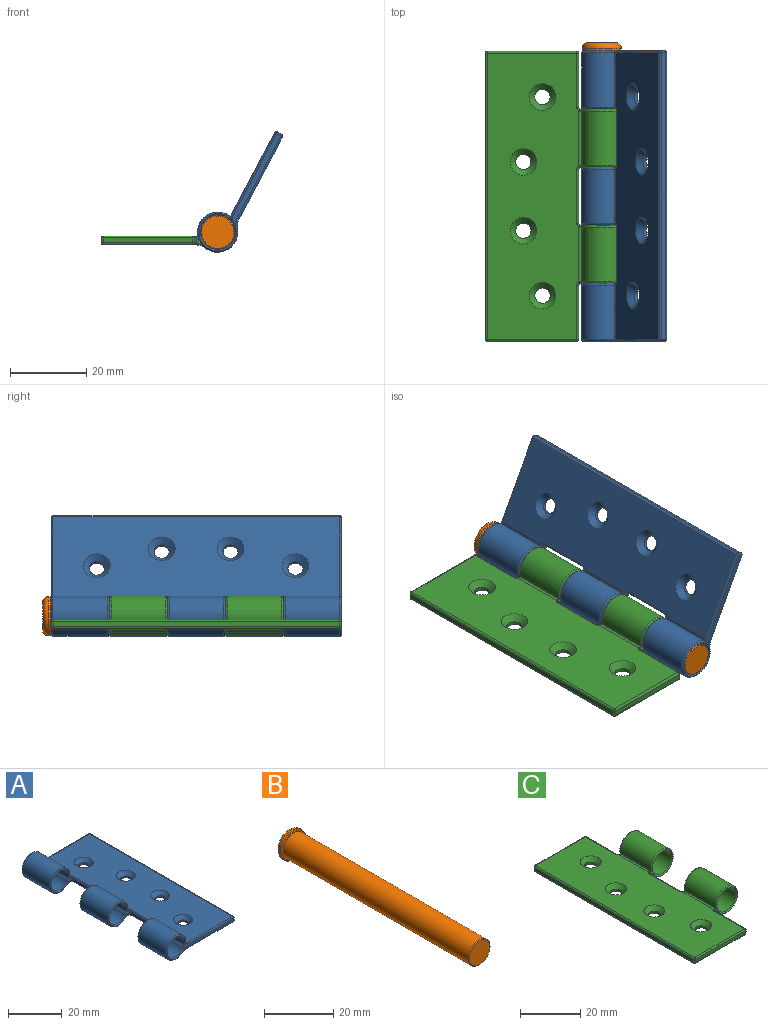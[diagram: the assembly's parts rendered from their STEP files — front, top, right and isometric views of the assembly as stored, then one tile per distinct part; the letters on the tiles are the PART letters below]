
ASSEMBLY  parts=3 mates=2
PART A: 94 faces, bbox 36.3x76x11.6 mm
  f0: cylinder r=5.25mm len=14.2mm, axis (0,1,0), area 412.4mm2, adj f2,f8,f69,f87
  f1: cylinder r=5.25mm len=14.2mm, axis (0,1,0), area 412.4mm2, adj f3,f9,f46,f78
  f2: plane 15.21x0.8mm, normal (0,0,-1), area 11.4mm2, adj f0,f4,f69,f71,f87,f90
  f3: plane 15.21x0.8mm, normal (0,0,-1), area 11.4mm2, adj f1,f5,f45,f46,f78,f80
  f4: cylinder r=4.5mm len=14.2mm, axis (0,1,0), area 382.9mm2, adj f2,f6,f71,f90
  f5: cylinder r=4.5mm len=14.2mm, axis (0,1,0), area 382.9mm2, adj f3,f7,f45,f80
  f6: cylinder r=2.39mm len=14.47mm, axis (0,1,0), area 36mm2, adj f4,f14,f73,f75,f92,f93
  f7: cylinder r=2.39mm len=14.33mm, axis (0,1,0), area 35.9mm2, adj f5,f14,f43,f82,f84
  f8: cylinder r=4.96mm len=14.47mm, axis (0,1,0), area 44.3mm2, adj f0,f16,f66,f68,f85,f88
  f9: cylinder r=4.96mm len=14.33mm, axis (0,1,0), area 44.3mm2, adj f1,f16,f48,f76,f77
  f10: cylinder r=5.25mm len=14.2mm, axis (0,1,0), area 412.4mm2, adj f11,f17,f51,f60
  f11: plane 15.21x0.8mm, normal (0,0,-1), area 11.4mm2, adj f10,f12,f51,f52,f60,f63
  f12: cylinder r=4.5mm len=14.2mm, axis (0,1,0), area 382.9mm2, adj f11,f13,f52,f63
  f13: cylinder r=2.39mm len=14.33mm, axis (0,1,0), area 35.9mm2, adj f12,f14,f49,f65,f67
  f14: plane 75x24mm, normal (0,0,1), area 1630.6mm2, adj f6,f7,f13,f21,f23,f25,f27,f41
  f15: plane 75x1.3mm, normal (1,0,0), area 97.5mm2, adj f38,f39,f42,f55
  f16: plane 75x24mm, normal (0,0,-1), area 1734.3mm2, adj f8,f9,f17,f20,f22,f24,f26,f50
  f17: cylinder r=4.96mm len=14.33mm, axis (0,1,0), area 44.3mm2, adj f10,f16,f54,f58,f61
  f18: plane 26.22x1.77mm, normal (0,-1,0), area 33.2mm2, adj f39,f47,f49,f52,f54,f56
  f19: plane 26.22x1.77mm, normal (0,1,0), area 33.2mm2, adj f38,f41,f43,f45,f48,f50
  f20: cylinder r=2mm len=4mm, axis (0,0,1), area 10.1mm2, adj f16,f21
  f21: cone r=2mm half-angle=45deg, axis (0,0,1), area 36.7mm2, adj f14,f20
  f22: cylinder r=2mm len=4mm, axis (0,0,1), area 10.1mm2, adj f16,f23
  f23: cone r=2mm half-angle=45deg, axis (0,0,1), area 36.7mm2, adj f14,f22
  f24: cylinder r=2mm len=4mm, axis (0,0,1), area 10.1mm2, adj f16,f25
  f25: cone r=2mm half-angle=45deg, axis (0,0,1), area 36.7mm2, adj f14,f24
  f26: cylinder r=2mm len=4mm, axis (0,0,1), area 10.1mm2, adj f16,f27
  f27: cone r=2mm half-angle=45deg, axis (0,0,1), area 36.7mm2, adj f14,f26
  f28: plane 14.2x1.3mm, normal (-1,0,0), area 18.5mm2, adj f34,f35,f81,f89
  f29: plane 1.72x1.7mm, normal (0,-1,0), area 1.3mm2, adj f34,f77,f80,f82
  f30: plane 1.72x1.7mm, normal (0,1,0), area 1.3mm2, adj f35,f88,f90,f92
  f31: plane 14.2x1.3mm, normal (-1,0,0), area 18.5mm2, adj f36,f37,f62,f72
  f32: plane 1.72x1.7mm, normal (0,1,0), area 1.3mm2, adj f36,f61,f63,f65
  f33: plane 1.72x1.7mm, normal (0,-1,0), area 1.3mm2, adj f37,f68,f71,f73
  f34: cylinder r=0.5mm len=1.32mm, axis (0,0,-1), area 1mm2, adj f28,f29,f76,f79,f84,f86
  f35: cylinder r=0.5mm len=1.32mm, axis (0,0,1), area 1mm2, adj f28,f30,f83,f85,f91,f93
  f36: cylinder r=0.5mm len=1.32mm, axis (0,0,-1), area 1mm2, adj f31,f32,f58,f59,f67,f70
  f37: cylinder r=0.5mm len=1.32mm, axis (0,0,1), area 1mm2, adj f31,f33,f64,f66,f74,f75
  f38: cylinder r=0.5mm len=1.3mm, axis (0,0,-1), area 1mm2, adj f15,f19,f40,f53
  f39: cylinder r=0.5mm len=1.3mm, axis (0,0,1), area 1mm2, adj f15,f18,f44,f57
  f40: sphere r=0.5mm, area 0.4mm2, adj f38,f41,f42
  f41: cylinder r=0.5mm len=24mm, axis (1,0,0), area 18.8mm2, adj f14,f19,f40,f43
  f42: cylinder r=0.5mm len=75mm, axis (0,1,0), area 58.9mm2, adj f14,f15,f40,f44
  f43: torus R=1.89mm, axis (0,-1,0), area 1.8mm2, adj f7,f19,f41,f45
  f44: sphere r=0.5mm, area 0.4mm2, adj f39,f42,f47
  f45: torus R=5mm, axis (0,-1,0), area 18.5mm2, adj f3,f5,f19,f43,f46,f48
  f46: torus R=4.75mm, axis (0,-1,0), area 18.7mm2, adj f1,f3,f45,f48
  f47: cylinder r=0.5mm len=24mm, axis (-1,0,0), area 18.8mm2, adj f14,f18,f44,f49
  f48: torus R=5.46mm, axis (0,-1,0), area 2.5mm2, adj f9,f19,f45,f46,f50
  f49: torus R=1.89mm, axis (0,-1,0), area 1.8mm2, adj f13,f18,f47,f52
  f50: cylinder r=0.5mm len=24mm, axis (-1,0,0), area 18.8mm2, adj f16,f19,f48,f53
  f51: torus R=4.75mm, axis (0,-1,0), area 18.7mm2, adj f10,f11,f52,f54
  f52: torus R=5mm, axis (0,-1,0), area 18.5mm2, adj f11,f12,f18,f49,f51,f54
  f53: sphere r=0.5mm, area 0.4mm2, adj f38,f50,f55
  f54: torus R=5.46mm, axis (0,-1,0), area 2.5mm2, adj f17,f18,f51,f52,f56
  f55: cylinder r=0.5mm len=75mm, axis (0,1,0), area 58.9mm2, adj f15,f16,f53,f57
  f56: cylinder r=0.5mm len=24mm, axis (1,0,0), area 18.8mm2, adj f16,f18,f54,f57
  f57: sphere r=0.5mm, area 0.4mm2, adj f39,f55,f56
  f58: bspline ~0.72x0.61mm, area 0.3mm2, adj f17,f36,f59,f61
  f59: torus R=1mm, axis (0,0,1), area 0.6mm2, adj f16,f36,f58,f62
  f60: torus R=4.75mm, axis (0,-1,0), area 18.7mm2, adj f10,f11,f61,f63
  f61: torus R=5.46mm, axis (0,-1,0), area 2.1mm2, adj f17,f32,f58,f60,f63
  f62: cylinder r=0.5mm len=14.2mm, axis (0,-1,0), area 11.2mm2, adj f16,f31,f59,f64
  f63: torus R=5mm, axis (0,-1,0), area 18.5mm2, adj f11,f12,f32,f60,f61,f65
  f64: torus R=1mm, axis (0,0,1), area 0.6mm2, adj f16,f37,f62,f66
  f65: torus R=1.89mm, axis (0,-1,0), area 1.4mm2, adj f13,f32,f63,f67
  f66: bspline ~0.72x0.61mm, area 0.3mm2, adj f8,f37,f64,f68
  f67: bspline ~0.83x0.6mm, area 0.3mm2, adj f13,f36,f65,f70
  f68: torus R=5.46mm, axis (0,-1,0), area 2.1mm2, adj f8,f33,f66,f69,f71
  f69: torus R=4.75mm, axis (0,-1,0), area 18.7mm2, adj f0,f2,f68,f71
  f70: torus R=1mm, axis (0,0,-1), area 0.6mm2, adj f14,f36,f67,f72
  f71: torus R=5mm, axis (0,-1,0), area 18.5mm2, adj f2,f4,f33,f68,f69,f73
  f72: cylinder r=0.5mm len=14.2mm, axis (0,-1,0), area 11.2mm2, adj f14,f31,f70,f74
  f73: torus R=1.89mm, axis (0,-1,0), area 1.4mm2, adj f6,f33,f71,f75
  f74: torus R=1mm, axis (0,0,-1), area 0.6mm2, adj f14,f37,f72,f75
  f75: bspline ~0.83x0.6mm, area 0.3mm2, adj f6,f37,f73,f74
  f76: bspline ~0.72x0.61mm, area 0.3mm2, adj f9,f34,f77,f79
  f77: torus R=5.46mm, axis (0,-1,0), area 2.1mm2, adj f9,f29,f76,f78,f80
  f78: torus R=4.75mm, axis (0,-1,0), area 18.7mm2, adj f1,f3,f77,f80
  f79: torus R=1mm, axis (0,0,1), area 0.6mm2, adj f16,f34,f76,f81
  f80: torus R=5mm, axis (0,-1,0), area 18.5mm2, adj f3,f5,f29,f77,f78,f82
  f81: cylinder r=0.5mm len=14.2mm, axis (0,1,0), area 11.2mm2, adj f16,f28,f79,f83
  f82: torus R=1.89mm, axis (0,-1,0), area 1.4mm2, adj f7,f29,f80,f84
  f83: torus R=1mm, axis (0,0,1), area 0.6mm2, adj f16,f35,f81,f85
  f84: bspline ~0.83x0.6mm, area 0.3mm2, adj f7,f34,f82,f86
  f85: bspline ~0.72x0.61mm, area 0.3mm2, adj f8,f35,f83,f88
  f86: torus R=1mm, axis (0,0,-1), area 0.6mm2, adj f14,f34,f84,f89
  f87: torus R=4.75mm, axis (0,-1,0), area 18.7mm2, adj f0,f2,f88,f90
  f88: torus R=5.46mm, axis (0,-1,0), area 2.1mm2, adj f8,f30,f85,f87,f90
  f89: cylinder r=0.5mm len=14.2mm, axis (0,-1,0), area 11.2mm2, adj f14,f28,f86,f91
  f90: torus R=5mm, axis (0,-1,0), area 18.5mm2, adj f2,f4,f30,f87,f88,f92
  f91: torus R=1mm, axis (0,0,-1), area 0.6mm2, adj f14,f35,f89,f93
  f92: torus R=1.89mm, axis (0,-1,0), area 1.4mm2, adj f6,f30,f90,f93
  f93: bspline ~0.83x0.6mm, area 0.3mm2, adj f6,f35,f91,f92
PART B: 8 faces, bbox 11x78.2x11 mm
  f0: cylinder r=4.4mm len=75.8mm, axis (0,1,0), area 2095.6mm2, adj f2,f5
  f1: plane 8.4x8.4mm, normal (0,-1,0), area 55.4mm2, adj f2
  f2: torus R=4.2mm, axis (0,-1,0), area 8.5mm2, adj f0,f1
  f3: cylinder r=5.1mm len=10.21mm, axis (0,-1,0), area 16mm2, adj f6,f7
  f4: plane 7.21x7.21mm, normal (0,1,0), area 40.8mm2, adj f6
  f5: plane 9.81x9.81mm, normal (0,-1,0), area 14.7mm2, adj f0,f7
  f6: torus R=3.6mm, axis (0,1,0), area 67.5mm2, adj f3,f4
  f7: torus R=4.9mm, axis (0,1,0), area 9.9mm2, adj f3,f5
PART C: 90 faces, bbox 36.3x76x11.6 mm
  f0: cylinder r=5.25mm len=14.2mm, axis (0,1,0), area 412.4mm2, adj f2,f8,f59,f83
  f1: cylinder r=5.25mm len=14.2mm, axis (0,1,0), area 412.4mm2, adj f3,f9,f46,f74
  f2: plane 15.21x0.8mm, normal (0,0,-1), area 11.4mm2, adj f0,f4,f59,f61,f83,f86
  f3: plane 15.21x0.8mm, normal (0,0,-1), area 11.4mm2, adj f1,f5,f46,f49,f74,f76
  f4: cylinder r=4.5mm len=14.2mm, axis (0,1,0), area 382.9mm2, adj f2,f6,f61,f86
  f5: cylinder r=4.5mm len=14.2mm, axis (0,1,0), area 382.9mm2, adj f3,f7,f49,f76
  f6: cylinder r=2.39mm len=14.47mm, axis (0,1,0), area 36mm2, adj f4,f10,f63,f65,f88,f89
  f7: cylinder r=2.39mm len=14.47mm, axis (0,1,0), area 36mm2, adj f5,f10,f51,f53,f78,f80
  f8: cylinder r=4.96mm len=14.47mm, axis (0,1,0), area 44.3mm2, adj f0,f12,f56,f58,f81,f84
  f9: cylinder r=4.96mm len=14.47mm, axis (0,1,0), area 44.3mm2, adj f1,f12,f44,f47,f72,f73
  f10: plane 75x24mm, normal (0,0,1), area 1623.5mm2, adj f6,f7,f16,f18,f20,f22,f55,f57
  f11: plane 75x1.3mm, normal (-1,0,0), area 97.5mm2, adj f36,f37,f43,f66
  f12: plane 75x24mm, normal (0,0,-1), area 1727.2mm2, adj f8,f9,f15,f17,f19,f21,f39,f40
  f13: plane 23.5x1.3mm, normal (0,-1,0), area 30.6mm2, adj f30,f37,f39,f62
  f14: plane 23.5x1.3mm, normal (0,1,0), area 30.6mm2, adj f34,f36,f48,f70
  f15: cylinder r=2mm len=4mm, axis (0,0,1), area 10.1mm2, adj f12,f16
  f16: cone r=2mm half-angle=45deg, axis (0,0,1), area 36.7mm2, adj f10,f15
  f17: cylinder r=2mm len=4mm, axis (0,0,1), area 10.1mm2, adj f12,f18
  f18: cone r=2mm half-angle=45deg, axis (0,0,1), area 36.7mm2, adj f10,f17
  f19: cylinder r=2mm len=4mm, axis (0,0,1), area 10.1mm2, adj f12,f20
  f20: cone r=2mm half-angle=45deg, axis (0,0,1), area 36.7mm2, adj f10,f19
  f21: cylinder r=2mm len=4mm, axis (0,0,1), area 10.1mm2, adj f12,f22
  f22: cone r=2mm half-angle=45deg, axis (0,0,1), area 36.7mm2, adj f10,f21
  f23: plane 14.2x1.3mm, normal (1,0,0), area 18.5mm2, adj f30,f31,f40,f57
  f24: plane 1.72x1.7mm, normal (0,-1,0), area 1.3mm2, adj f31,f47,f49,f51
  f25: plane 14.2x1.3mm, normal (1,0,0), area 18.5mm2, adj f32,f33,f77,f85
  f26: plane 1.72x1.7mm, normal (0,1,0), area 1.3mm2, adj f32,f73,f76,f78
  f27: plane 1.72x1.7mm, normal (0,-1,0), area 1.3mm2, adj f33,f84,f86,f88
  f28: plane 14.2x1.3mm, normal (1,0,0), area 18.5mm2, adj f34,f35,f52,f69
  f29: plane 1.72x1.7mm, normal (0,1,0), area 1.3mm2, adj f35,f58,f61,f63
  f30: cylinder r=0.5mm len=1.3mm, axis (0,0,1), area 1mm2, adj f13,f23,f38,f60
  f31: cylinder r=0.5mm len=1.32mm, axis (0,0,1), area 1mm2, adj f23,f24,f42,f44,f53,f55
  f32: cylinder r=0.5mm len=1.32mm, axis (0,0,-1), area 1mm2, adj f25,f26,f72,f75,f80,f82
  f33: cylinder r=0.5mm len=1.32mm, axis (0,0,1), area 1mm2, adj f25,f27,f79,f81,f87,f89
  f34: cylinder r=0.5mm len=1.3mm, axis (0,0,-1), area 1mm2, adj f14,f28,f50,f71
  f35: cylinder r=0.5mm len=1.32mm, axis (0,0,-1), area 1mm2, adj f28,f29,f54,f56,f65,f67
  f36: cylinder r=0.5mm len=1.3mm, axis (0,0,-1), area 1mm2, adj f11,f14,f45,f68
  f37: cylinder r=0.5mm len=1.3mm, axis (0,0,1), area 1mm2, adj f11,f13,f41,f64
  f38: sphere r=0.5mm, area 0.4mm2, adj f30,f39,f40
  f39: cylinder r=0.5mm len=23.5mm, axis (-1,0,0), area 18.5mm2, adj f12,f13,f38,f41
  f40: cylinder r=0.5mm len=14.2mm, axis (0,1,0), area 11.2mm2, adj f12,f23,f38,f42
  f41: sphere r=0.5mm, area 0.4mm2, adj f37,f39,f43
  f42: torus R=1mm, axis (0,0,1), area 0.6mm2, adj f12,f31,f40,f44
  f43: cylinder r=0.5mm len=75mm, axis (0,1,0), area 58.9mm2, adj f11,f12,f41,f45
  f44: bspline ~0.72x0.61mm, area 0.3mm2, adj f9,f31,f42,f47
  f45: sphere r=0.5mm, area 0.4mm2, adj f36,f43,f48
  f46: torus R=4.75mm, axis (0,1,0), area 18.7mm2, adj f1,f3,f47,f49
  f47: torus R=5.46mm, axis (0,1,0), area 2.1mm2, adj f9,f24,f44,f46,f49
  f48: cylinder r=0.5mm len=23.5mm, axis (1,0,0), area 18.5mm2, adj f12,f14,f45,f50
  f49: torus R=5mm, axis (0,1,0), area 18.5mm2, adj f3,f5,f24,f46,f47,f51
  f50: sphere r=0.5mm, area 0.4mm2, adj f34,f48,f52
  f51: torus R=1.89mm, axis (0,1,0), area 1.4mm2, adj f7,f24,f49,f53
  f52: cylinder r=0.5mm len=14.2mm, axis (0,-1,0), area 11.2mm2, adj f12,f28,f50,f54
  f53: bspline ~0.83x0.6mm, area 0.3mm2, adj f7,f31,f51,f55
  f54: torus R=1mm, axis (0,0,1), area 0.6mm2, adj f12,f35,f52,f56
  f55: torus R=1mm, axis (0,0,-1), area 0.6mm2, adj f10,f31,f53,f57
  f56: bspline ~0.72x0.61mm, area 0.3mm2, adj f8,f35,f54,f58
  f57: cylinder r=0.5mm len=14.2mm, axis (0,1,0), area 11.2mm2, adj f10,f23,f55,f60
  f58: torus R=5.46mm, axis (0,1,0), area 2.1mm2, adj f8,f29,f56,f59,f61
  f59: torus R=4.75mm, axis (0,1,0), area 18.7mm2, adj f0,f2,f58,f61
  f60: sphere r=0.5mm, area 0.4mm2, adj f30,f57,f62
  f61: torus R=5mm, axis (0,1,0), area 18.5mm2, adj f2,f4,f29,f58,f59,f63
  f62: cylinder r=0.5mm len=23.5mm, axis (1,0,0), area 18.5mm2, adj f10,f13,f60,f64
  f63: torus R=1.89mm, axis (0,1,0), area 1.4mm2, adj f6,f29,f61,f65
  f64: sphere r=0.5mm, area 0.4mm2, adj f37,f62,f66
  f65: bspline ~0.83x0.6mm, area 0.3mm2, adj f6,f35,f63,f67
  f66: cylinder r=0.5mm len=75mm, axis (0,1,0), area 58.9mm2, adj f10,f11,f64,f68
  f67: torus R=1mm, axis (0,0,-1), area 0.6mm2, adj f10,f35,f65,f69
  f68: sphere r=0.5mm, area 0.4mm2, adj f36,f66,f70
  f69: cylinder r=0.5mm len=14.2mm, axis (0,1,0), area 11.2mm2, adj f10,f28,f67,f71
  f70: cylinder r=0.5mm len=23.5mm, axis (-1,0,0), area 18.5mm2, adj f10,f14,f68,f71
  f71: sphere r=0.5mm, area 0.4mm2, adj f34,f69,f70
  f72: bspline ~0.72x0.61mm, area 0.3mm2, adj f9,f32,f73,f75
  f73: torus R=5.46mm, axis (0,1,0), area 2.1mm2, adj f9,f26,f72,f74,f76
  f74: torus R=4.75mm, axis (0,1,0), area 18.7mm2, adj f1,f3,f73,f76
  f75: torus R=1mm, axis (0,0,1), area 0.6mm2, adj f12,f32,f72,f77
  f76: torus R=5mm, axis (0,1,0), area 18.5mm2, adj f3,f5,f26,f73,f74,f78
  f77: cylinder r=0.5mm len=14.2mm, axis (0,1,0), area 11.2mm2, adj f12,f25,f75,f79
  f78: torus R=1.89mm, axis (0,1,0), area 1.4mm2, adj f7,f26,f76,f80
  f79: torus R=1mm, axis (0,0,1), area 0.6mm2, adj f12,f33,f77,f81
  f80: bspline ~0.83x0.6mm, area 0.3mm2, adj f7,f32,f78,f82
  f81: bspline ~0.72x0.61mm, area 0.3mm2, adj f8,f33,f79,f84
  f82: torus R=1mm, axis (0,0,-1), area 0.6mm2, adj f10,f32,f80,f85
  f83: torus R=4.75mm, axis (0,1,0), area 18.7mm2, adj f0,f2,f84,f86
  f84: torus R=5.46mm, axis (0,1,0), area 2.1mm2, adj f8,f27,f81,f83,f86
  f85: cylinder r=0.5mm len=14.2mm, axis (0,1,0), area 11.2mm2, adj f10,f25,f82,f87
  f86: torus R=5mm, axis (0,1,0), area 18.5mm2, adj f2,f4,f27,f83,f84,f88
  f87: torus R=1mm, axis (0,0,-1), area 0.6mm2, adj f10,f33,f85,f89
  f88: torus R=1.89mm, axis (0,1,0), area 1.4mm2, adj f6,f27,f86,f89
  f89: bspline ~0.83x0.6mm, area 0.3mm2, adj f6,f33,f87,f88
PLACE A rot(axis=(0,-1,0),62deg) t=(11.7,-5.85,-6.91)mm
PLACE B t=(7.63,-5.83,-2.14)mm
PLACE C t=(7.63,-5.88,-2.14)mm fixed
MATE revolute C.f0 <-> A.f0  axis (0,1,0) through (13.63,-66.66,-1.14)mm
MATE revolute B.f0 <-> A.f0  axis (0,-1,0) through (13.63,-81.83,-1.14)mm
